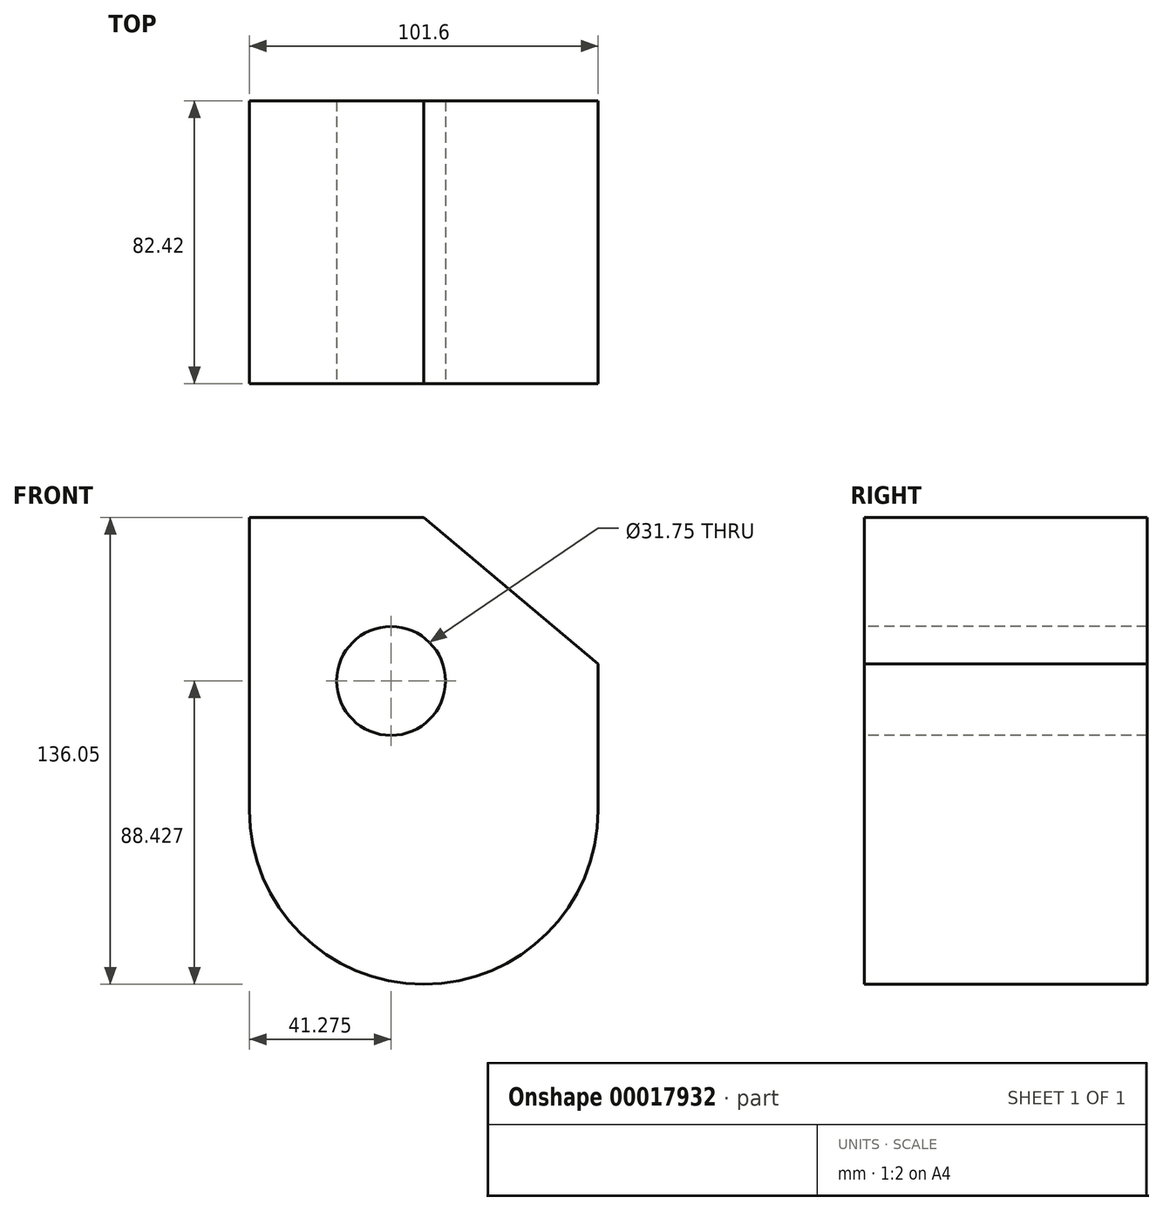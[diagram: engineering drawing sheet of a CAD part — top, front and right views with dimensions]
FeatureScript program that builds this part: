
annotation { "Feature Type Name" : "Feature", "Feature Type Description" : "" }
export const myFeature = defineFeature(function(context is Context, id is Id, definition is map)
    precondition{}
    {
        {
            var Q0;
            Q0=qCreatedBy(makeId("Front.planeOp"),FACE);
            var sketch = newSketch(context, id + "F0", { "sketchPlane" : qUnion([Q0])});
            skLineSegment(sketch, "E0.top", {"start": v(0, 85.25) * mm, "end": v(50.8, 85.25) * mm});
            skLineSegment(sketch, "E0.left", {"start": v(0, 0) * mm, "end": v(0, 85.25) * mm});
            skLineSegment(sketch, "E0.right", {"start": v(101.6, 0) * mm, "end": v(101.6, 42.63) * mm});
            skLineSegment(sketch, "E1", {"start": v(50.8, 85.25) * mm, "end": v(101.6, 42.63) * mm});
            skPoint(sketch, "E2.orphan", {"position": v(101.6, 85.25) * mm});
            skCircle(sketch, "E3", {"center": v(41.27, 37.63) * mm, "radius": 15.88 * mm});
            skArc(sketch, "E4", {"start": v(0, 0) * mm, "mid": v(50.8, -50.8) * mm, "end": v(101.6, 0) * mm});
            skSolve(sketch);
        }
        {
            var Q0;
            Q0=makeQuery(id+"F0.imprint","IMPRINT",FACE,{"disambiguationData":[TD([[makeQuery(id+"F0.imprint","IMPRINT",EDGE,{"derivedFrom":sQuery(id+"F0.wireOp",EDGE,"E0.top")}),-1.0]])]});
            extrude(context, id + "F1", {"entities" : qUnion([Q0]), "oppositeDirection" : true, "depth" : 82.42 * mm});
        }
    });
